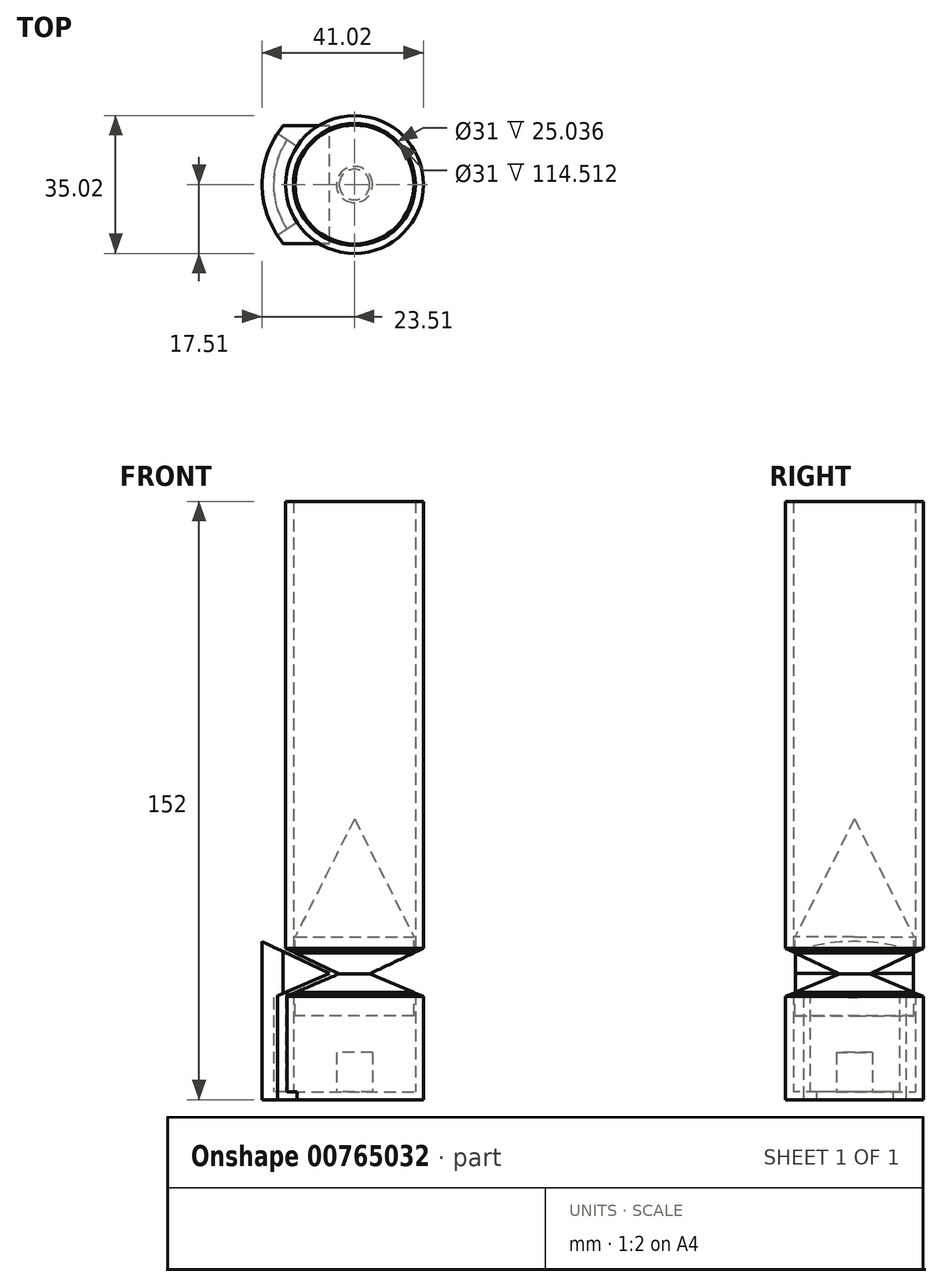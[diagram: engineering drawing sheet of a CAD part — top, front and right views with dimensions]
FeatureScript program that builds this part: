
annotation { "Feature Type Name" : "Feature", "Feature Type Description" : "" }
export const myFeature = defineFeature(function(context is Context, id is Id, definition is map)
    precondition{}
    {
        {
            var Q0;
            Q0=qCreatedBy(makeId("Top.planeOp"),FACE);
            var sketch = newSketch(context, id + "F0", { "sketchPlane" : qUnion([Q0])});
            skCircle(sketch, "E0", {"center": v(0, 0) * mm, "radius": 17.5 * mm});
            skCircle(sketch, "E1", {"center": v(0, 0) * mm, "radius": 4.6 * mm});
            skSolve(sketch);
        }
        {
            var Q0;
            Q0 = qSketchRegion(id + "F0", true);
            var Q1;
            Q1=makeQuery(id+"F0.imprint","IMPRINT",FACE,{"disambiguationData":[TD([[makeQuery(id+"F0.imprint","IMPRINT",EDGE,{"derivedFrom":sQuery(id+"F0.wireOp",EDGE,"E1")}),1.0]])]});
            extrude(context, id + "F1", {"entities" : qUnion([Q0, Q1]), "depth" : 2 * mm, "offsetDistance" : 25 * mm});
        }
        {
            var Q0;
            Q0=makeQuery(id+"F0.imprint","IMPRINT",FACE,{"disambiguationData":[TD([[makeQuery(id+"F0.imprint","IMPRINT",EDGE,{"derivedFrom":sQuery(id+"F0.wireOp",EDGE,"E1")}),1.0]])]});
            extrude(context, id + "F2", {"entities" : qUnion([Q0]), "operationType" : NewBodyOperationType.ADD, "depth" : 12 * mm, "offsetDistance" : 25 * mm});
        }
        {
            var Q0;
            Q0=makeQuery(id+"F1.opExtrude","CAP_FACE",FACE,{"disambiguationData":[OSD([sQuery(id+"F0.wireOp",EDGE,"E0")])],"isStart":false});
            var sketch = newSketch(context, id + "F3", { "sketchPlane" : qUnion([Q0])});
            skCircle(sketch, "E2.0", {"center": v(0, 0) * mm, "radius": 15.5 * mm});
            skSolve(sketch);
        }
        {
            var Q0;
            Q0=makeQuery(id+"F3.imprint","IMPRINT",FACE,{"disambiguationData":[TD([[makeQuery(id+"F3.imprint","IMPRINT",EDGE,{"derivedFrom":sQuery(id+"F3.wireOp",EDGE,"E2.0")}),-1.0]])]});
            extrude(context, id + "F4", {"entities" : qUnion([Q0]), "operationType" : NewBodyOperationType.ADD, "depth" : 150 * mm, "offsetDistance" : 25 * mm});
        }
        {
            var Q0;
            Q0=qCreatedBy(makeId("Front.planeOp"),FACE);
            var sketch = newSketch(context, id + "F5", { "sketchPlane" : qUnion([Q0])});
            skLineSegment(sketch, "E3", {"start": v(15.1, 21.33) * mm, "end": v(15.1, 41.33) * mm});
            skLineSegment(sketch, "E4", {"start": v(15.1, 41.33) * mm, "end": v(0, 71.33) * mm});
            skLineSegment(sketch, "E5", {"start": v(0, 71.33) * mm, "end": v(-15.1, 41.33) * mm});
            skLineSegment(sketch, "E6", {"start": v(-15.1, 41.33) * mm, "end": v(-15.1, 21.33) * mm});
            skLineSegment(sketch, "E7", {"start": v(-15.1, 21.33) * mm, "end": v(0, 21.33) * mm});
            skLineSegment(sketch, "E8", {"start": v(0, 21.33) * mm, "end": v(15.1, 21.33) * mm});
            skLineSegment(sketch, "E9", {"start": v(0, 71.33) * mm, "end": v(0, 21.33) * mm});
            skSolve(sketch);
        }
        {
            var Q0;
            Q0=makeQuery(id+"F5.imprint","IMPRINT",FACE,{"disambiguationData":[TD([[makeQuery(id+"F5.imprint","IMPRINT",EDGE,{"derivedFrom":sQuery(id+"F5.wireOp",EDGE,"E3")}),1.0]])]});
            var Q1;
            Q1=sQuery(id+"F5.wireOp",EDGE,"E9");
            revolve(context, id + "F6", {"surfaceOperationType" : NewSurfaceOperationType.NEW, "entities" : qUnion([Q0]), "axis" : qUnion([Q1]), "revolveType" : RevolveType.FULL});
        }
        {
            var Q0;
            Q0=qCreatedBy(makeId("Front.planeOp"),FACE);
            var sketch = newSketch(context, id + "F7", { "sketchPlane" : qUnion([Q0])});
            skLineSegment(sketch, "E10", {"start": v(-26.1, 42.52) * mm, "end": v(-3.89, 31.98) * mm});
            skLineSegment(sketch, "E11", {"start": v(-3.89, 31.98) * mm, "end": v(-26.1, 22.52) * mm});
            skLineSegment(sketch, "E12", {"start": v(-26.1, 22.52) * mm, "end": v(-26.1, 42.52) * mm});
            skLineSegment(sketch, "E13.0", {"start": v(-6.33, 32.03) * mm, "end": v(-23.03, 24.91) * mm});
            skLineSegment(sketch, "E13.1", {"start": v(-26.03, 41.37) * mm, "end": v(-6.33, 32.03) * mm});
            skLineSegment(sketch, "E14", {"start": v(-23.03, 24.91) * mm, "end": v(-30.5, 21.73) * mm});
            skLineSegment(sketch, "E15", {"start": v(-26.03, 41.37) * mm, "end": v(-30.52, 42.9) * mm});
            skSolve(sketch);
        }
        {
            var Q0;
            {var subQ1=sQuery(id+"F7.wireOp",EDGE,"E13.0");Q0=makeQuery(id+"F7.imprint","IMPRINT",FACE,{"disambiguationData":[TD([[makeQuery(id+"F7.imprint","IMPRINT",EDGE,{"derivedFrom":subQ1}),-1.0]])]});}
            var Q1;
            {var subQ1=sQuery(id+"F7.wireOp",EDGE,"E10");Q1=makeQuery(id+"F7.imprint","IMPRINT",FACE,{"disambiguationData":[TD([[makeQuery(id+"F7.imprint","IMPRINT",EDGE,{"derivedFrom":subQ1}),-1.0]])]});}
            var Q2;
            Q2=sQuery(id+"F5.wireOp",EDGE,"E9");
            revolve(context, id + "F8", {"operationType" : NewBodyOperationType.REMOVE, "surfaceOperationType" : NewSurfaceOperationType.NEW, "entities" : qUnion([Q0, Q1]), "axis" : qUnion([Q2]), "revolveType" : RevolveType.FULL, "oppositeDirection" : true});
        }
        {
            var Q0;
            {var subQ1=sQuery(id+"F7.wireOp",EDGE,"E13.0");Q0=makeQuery(id+"F7.imprint","IMPRINT",FACE,{"disambiguationData":[TD([[makeQuery(id+"F7.imprint","IMPRINT",EDGE,{"derivedFrom":subQ1}),-1.0]])]});}
            var Q1;
            {var subQ1=sQuery(id+"F7.wireOp",EDGE,"E10");Q1=makeQuery(id+"F7.imprint","IMPRINT",FACE,{"disambiguationData":[TD([[makeQuery(id+"F7.imprint","IMPRINT",EDGE,{"derivedFrom":subQ1}),-1.0]])]});}
            extrude(context, id + "F9", {"entities" : qUnion([Q0, Q1]), "operationType" : NewBodyOperationType.REMOVE, "endBound" : BoundingType.SYMMETRIC, "oppositeDirection" : true, "depth" : 34 * mm, "offsetDistance" : 25 * mm});
        }
        {
            var Q0;
            {var subQ1=sQuery(id+"F7.wireOp",EDGE,"E13.0");Q0=makeQuery(id+"F7.imprint","IMPRINT",FACE,{"disambiguationData":[TD([[makeQuery(id+"F7.imprint","IMPRINT",EDGE,{"derivedFrom":subQ1}),-1.0]])]});}
            extrude(context, id + "F10", {"entities" : qUnion([Q0]), "operationType" : NewBodyOperationType.ADD, "endBound" : BoundingType.SYMMETRIC, "depth" : 30 * mm, "offsetDistance" : 25 * mm});
        }
        {
            var Q0;
            Q0=qCreatedBy(makeId("Top.planeOp"),FACE);
            var sketch = newSketch(context, id + "F11", { "sketchPlane" : qUnion([Q0])});
            skCircle(sketch, "E16.0", {"center": v(0, 0) * mm, "radius": 20.5 * mm});
            skCircle(sketch, "E17.0", {"center": v(0, 0) * mm, "radius": 23.5 * mm});
            skLineSegment(sketch, "E18", {"start": v(0, 0) * mm, "end": v(-41.07, -27.35) * mm});
            skLineSegment(sketch, "E19", {"start": v(-41.07, -27.35) * mm, "end": v(-41.07, 0) * mm});
            skLineSegment(sketch, "E20", {"start": v(-41.07, 0) * mm, "end": v(-41.07, 27.35) * mm});
            skLineSegment(sketch, "E21", {"start": v(-41.07, 27.35) * mm, "end": v(0, 0) * mm});
            skLineSegment(sketch, "E22", {"start": v(0, 0) * mm, "end": v(-29.54, 50.76) * mm});
            skLineSegment(sketch, "E23", {"start": v(-29.54, 50.76) * mm, "end": v(-73.55, -8.21) * mm});
            skLineSegment(sketch, "E24", {"start": v(-73.55, -8.21) * mm, "end": v(-56.2, -50.74) * mm});
            skLineSegment(sketch, "E25", {"start": v(-56.2, -50.74) * mm, "end": v(-31.76, -50.74) * mm});
            skLineSegment(sketch, "E26", {"start": v(-31.76, -50.74) * mm, "end": v(0, 0) * mm});
            skSolve(sketch);
        }
        {
            var Q0;
            {var subQ0=sQuery(id+"F11.wireOp",EDGE,"E18");var subQ1=sQuery(id+"F11.wireOp",EDGE,"E16.0");var subQ2=makeQuery(id+"F11.imprint","INTERSECT",VERTEX,{"derivedFrom":[subQ1,subQ0]});Q0=makeQuery(id+"F11.imprint","IMPRINT",FACE,{"disambiguationData":[TD([[makeQuery(id+"F11.imprint","IMPRINT",EDGE,{"disambiguationData":[TD([[subQ2,1.0]])],"derivedFrom":subQ1}),-1.0]])]});}
            var Q1;
            {var subQ0=sQuery(id+"F11.wireOp",EDGE,"E18");var subQ1=sQuery(id+"F11.wireOp",EDGE,"E16.0");var subQ2=makeQuery(id+"F11.imprint","INTERSECT",VERTEX,{"derivedFrom":[subQ1,subQ0]});Q1=makeQuery(id+"F11.imprint","IMPRINT",FACE,{"disambiguationData":[TD([[makeQuery(id+"F11.imprint","IMPRINT",EDGE,{"disambiguationData":[TD([[subQ2,1.0]])],"derivedFrom":subQ1}),1.0]])]});}
            extrude(context, id + "F12", {"entities" : qUnion([Q0, Q1]), "operationType" : NewBodyOperationType.ADD, "depth" : 2 * mm, "offsetDistance" : 25 * mm});
        }
        {
            var Q0;
            {var subQ0=sQuery(id+"F11.wireOp",EDGE,"E18");var subQ1=sQuery(id+"F11.wireOp",EDGE,"E16.0");var subQ2=makeQuery(id+"F11.imprint","INTERSECT",VERTEX,{"derivedFrom":[subQ1,subQ0]});Q0=makeQuery(id+"F11.imprint","IMPRINT",FACE,{"disambiguationData":[TD([[makeQuery(id+"F11.imprint","IMPRINT",EDGE,{"disambiguationData":[TD([[subQ2,1.0]])],"derivedFrom":subQ1}),-1.0]])]});}
            extrude(context, id + "F13", {"entities" : qUnion([Q0]), "operationType" : NewBodyOperationType.ADD, "depth" : 35 * mm, "offsetDistance" : 25 * mm});
        }
        {
            var Q0;
            {var subQ1=sQuery(id+"F11.wireOp",EDGE,"E19");Q0=makeQuery(id+"F11.imprint","IMPRINT",FACE,{"disambiguationData":[TD([[makeQuery(id+"F11.imprint","IMPRINT",EDGE,{"derivedFrom":subQ1}),-1.0]])]});}
            var Q1;
            {var subQ11=sQuery(id+"F11.wireOp",EDGE,"E19");Q1=makeQuery(id+"F11.imprint","IMPRINT",FACE,{"disambiguationData":[TD([[makeQuery(id+"F11.imprint","IMPRINT",EDGE,{"derivedFrom":subQ11}),1.0]])]});}
            extrude(context, id + "F14", {"entities" : qUnion([Q0, Q1]), "operationType" : NewBodyOperationType.REMOVE, "endBound" : BoundingType.THROUGH_ALL, "depth" : 25 * mm, "offsetDistance" : 25 * mm});
        }
    });
